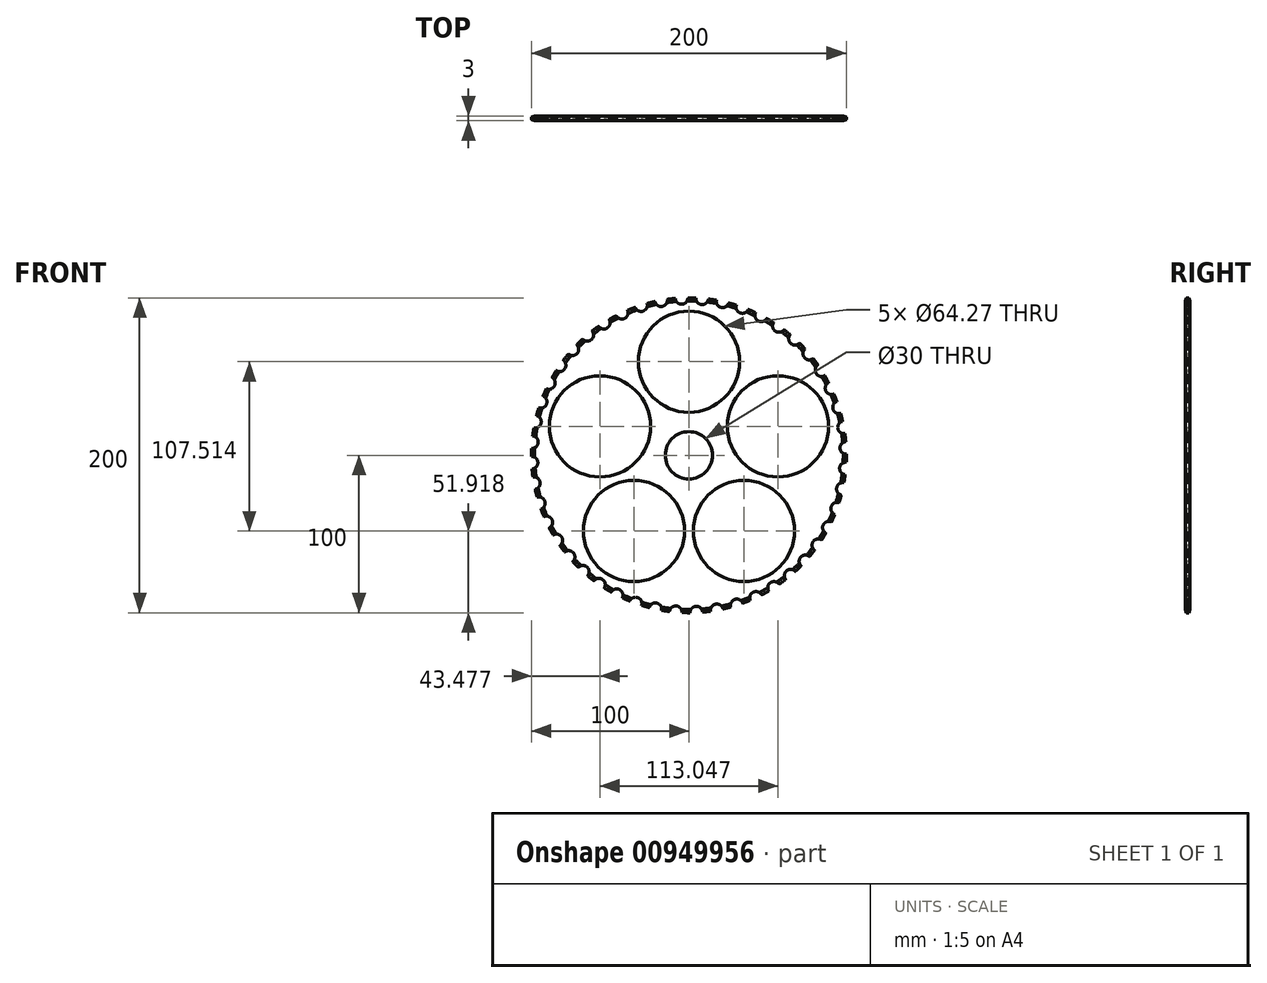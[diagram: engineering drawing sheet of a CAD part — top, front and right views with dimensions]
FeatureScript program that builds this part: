
annotation { "Feature Type Name" : "Feature", "Feature Type Description" : "" }
export const myFeature = defineFeature(function(context is Context, id is Id, definition is map)
    precondition{}
    {
        {
            var Q0;
            Q0=qCreatedBy(makeId("Front.planeOp"),FACE);
            var sketch = newSketch(context, id + "F0", { "sketchPlane" : qUnion([Q0])});
            skCircle(sketch, "E0", {"center": v(0, 0) * mm, "radius": 100 * mm});
            skCircle(sketch, "E1", {"center": v(0, 59.43) * mm, "radius": 32.14 * mm});
            skCircle(sketch, "E2.1.0", {"center": v(-56.52, 18.37) * mm, "radius": 32.14 * mm});
            skCircle(sketch, "E2.2.0", {"center": v(-34.93, -48.08) * mm, "radius": 32.14 * mm});
            skCircle(sketch, "E2.3.0", {"center": v(34.93, -48.08) * mm, "radius": 32.14 * mm});
            skCircle(sketch, "E2.4.0", {"center": v(56.52, 18.37) * mm, "radius": 32.14 * mm});
            skSolve(sketch);
        }
        {
            var Q0;
            Q0=makeQuery(id+"F0.imprint","IMPRINT",FACE,{"disambiguationData":[TD([[makeQuery(id+"F0.imprint","IMPRINT",EDGE,{"derivedFrom":sQuery(id+"F0.wireOp",EDGE,"E0")}),1.0]])]});
            extrude(context, id + "F1", {"entities" : qUnion([Q0]), "depth" : 3 * mm, "offsetDistance" : 25 * mm});
        }
        {
            var Q0;
            {var subQ0=sQuery(id+"F0.wireOp",EDGE,"E0");Q0=makeQuery(id+"FjPS6zSCau8WYdw_1.boolean.opBoolean","SPLIT",EDGE,{"disambiguationData":[TD([makeQuery(id+"F1.opExtrude","SWEPT_FACE",FACE,{"disambiguationData":[OSD([subQ0])]}),makeQuery(id+"F1.opExtrude","CAP_FACE",FACE,{"disambiguationData":[OSD([subQ0])],"isStart":false}),makeQuery(id+"FjPS6zSCau8WYdw_1.opExtrude","SWEPT_FACE",FACE,{"disambiguationData":[OSD([sQuery(id+"F4.wireOp",EDGE,"E4.5.0")])]}),makeQuery(id+"FjPS6zSCau8WYdw_1.opExtrude","SWEPT_FACE",FACE,{"disambiguationData":[OSD([sQuery(id+"F4.wireOp",EDGE,"E4.6.0")])]})])],"derivedFrom":makeQuery(id+"F1.opExtrude","CAP_EDGE",EDGE,{"disambiguationData":[OSD([subQ0])],"isStart":false})});}
            chamfer(context, id + "F2", {"entities" : qUnion([Q0]), "chamferType" : ChamferType.TWO_OFFSETS, "width1" : 2 * mm, "oppositeDirection" : false, "width2" : 0.75 * mm, "tangentPropagation" : true});
        }
        {
            var Q0;
            {var subQ0=sQuery(id+"F0.wireOp",EDGE,"E0");Q0=makeQuery(id+"FjPS6zSCau8WYdw_1.boolean.opBoolean","SPLIT",EDGE,{"disambiguationData":[TD([makeQuery(id+"F1.opExtrude","SWEPT_FACE",FACE,{"disambiguationData":[OSD([subQ0])]}),makeQuery(id+"F1.opExtrude","CAP_FACE",FACE,{"disambiguationData":[OSD([subQ0])],"isStart":true}),makeQuery(id+"FjPS6zSCau8WYdw_1.opExtrude","SWEPT_FACE",FACE,{"disambiguationData":[OSD([sQuery(id+"F4.wireOp",EDGE,"E4.21.0")])]}),makeQuery(id+"FjPS6zSCau8WYdw_1.opExtrude","SWEPT_FACE",FACE,{"disambiguationData":[OSD([sQuery(id+"F4.wireOp",EDGE,"E4.22.0")])]})])],"derivedFrom":makeQuery(id+"F1.opExtrude","CAP_EDGE",EDGE,{"disambiguationData":[OSD([subQ0])],"isStart":true})});}
            chamfer(context, id + "F3", {"entities" : qUnion([Q0]), "chamferType" : ChamferType.TWO_OFFSETS, "width1" : 0.75 * mm, "oppositeDirection" : false, "width2" : 2 * mm, "tangentPropagation" : true});
        }
        {
            var Q0;
            Q0=makeQuery(id+"F1.opExtrude","CAP_FACE",FACE,{"disambiguationData":[OSD([sQuery(id+"F0.wireOp",EDGE,"E0")])],"isStart":false});
            var sketch = newSketch(context, id + "F4", { "sketchPlane" : qUnion([Q0])});
            skCircle(sketch, "E3", {"center": v(-88.92, 45.9) * mm, "radius": 4 * mm});
            skCircle(sketch, "E4.1.0", {"center": v(-94.15, 33.9) * mm, "radius": 4 * mm});
            skCircle(sketch, "E4.2.0", {"center": v(-97.77, 21.33) * mm, "radius": 4 * mm});
            skCircle(sketch, "E4.3.0", {"center": v(-99.72, 8.38) * mm, "radius": 4 * mm});
            skCircle(sketch, "E4.4.0", {"center": v(-99.96, -4.7) * mm, "radius": 4 * mm});
            skCircle(sketch, "E4.5.0", {"center": v(-98.49, -17.7) * mm, "radius": 4 * mm});
            skCircle(sketch, "E4.6.0", {"center": v(-95.33, -30.41) * mm, "radius": 4 * mm});
            skCircle(sketch, "E4.7.0", {"center": v(-90.55, -42.6) * mm, "radius": 4 * mm});
            skCircle(sketch, "E4.8.0", {"center": v(-84.21, -54.05) * mm, "radius": 4 * mm});
            skCircle(sketch, "E4.9.0", {"center": v(-76.44, -64.58) * mm, "radius": 4 * mm});
            skCircle(sketch, "E4.10.0", {"center": v(-67.35, -74) * mm, "radius": 4 * mm});
            skCircle(sketch, "E4.11.0", {"center": v(-57.12, -82.16) * mm, "radius": 4 * mm});
            skCircle(sketch, "E4.12.0", {"center": v(-45.9, -88.92) * mm, "radius": 4 * mm});
            skCircle(sketch, "E4.13.0", {"center": v(-33.9, -94.15) * mm, "radius": 4 * mm});
            skCircle(sketch, "E4.14.0", {"center": v(-21.33, -97.77) * mm, "radius": 4 * mm});
            skCircle(sketch, "E4.15.0", {"center": v(-8.38, -99.72) * mm, "radius": 4 * mm});
            skCircle(sketch, "E4.16.0", {"center": v(4.7, -99.96) * mm, "radius": 4 * mm});
            skCircle(sketch, "E4.17.0", {"center": v(17.7, -98.49) * mm, "radius": 4 * mm});
            skCircle(sketch, "E4.18.0", {"center": v(30.41, -95.33) * mm, "radius": 4 * mm});
            skCircle(sketch, "E4.19.0", {"center": v(42.6, -90.55) * mm, "radius": 4 * mm});
            skCircle(sketch, "E4.20.0", {"center": v(54.05, -84.21) * mm, "radius": 4 * mm});
            skCircle(sketch, "E4.21.0", {"center": v(64.58, -76.44) * mm, "radius": 4 * mm});
            skCircle(sketch, "E4.22.0", {"center": v(74, -67.35) * mm, "radius": 4 * mm});
            skCircle(sketch, "E4.23.0", {"center": v(82.16, -57.12) * mm, "radius": 4 * mm});
            skCircle(sketch, "E4.24.0", {"center": v(88.92, -45.9) * mm, "radius": 4 * mm});
            skCircle(sketch, "E4.25.0", {"center": v(94.15, -33.9) * mm, "radius": 4 * mm});
            skCircle(sketch, "E4.26.0", {"center": v(97.77, -21.33) * mm, "radius": 4 * mm});
            skCircle(sketch, "E4.27.0", {"center": v(99.72, -8.38) * mm, "radius": 4 * mm});
            skCircle(sketch, "E4.28.0", {"center": v(99.96, 4.7) * mm, "radius": 4 * mm});
            skCircle(sketch, "E4.29.0", {"center": v(98.49, 17.7) * mm, "radius": 4 * mm});
            skCircle(sketch, "E4.30.0", {"center": v(95.33, 30.41) * mm, "radius": 4 * mm});
            skCircle(sketch, "E4.31.0", {"center": v(90.55, 42.6) * mm, "radius": 4 * mm});
            skCircle(sketch, "E4.32.0", {"center": v(84.21, 54.05) * mm, "radius": 4 * mm});
            skCircle(sketch, "E4.33.0", {"center": v(76.44, 64.58) * mm, "radius": 4 * mm});
            skCircle(sketch, "E4.34.0", {"center": v(67.35, 74) * mm, "radius": 4 * mm});
            skCircle(sketch, "E4.35.0", {"center": v(57.12, 82.16) * mm, "radius": 4 * mm});
            skCircle(sketch, "E4.36.0", {"center": v(45.9, 88.92) * mm, "radius": 4 * mm});
            skCircle(sketch, "E4.37.0", {"center": v(33.9, 94.15) * mm, "radius": 4 * mm});
            skCircle(sketch, "E4.38.0", {"center": v(21.33, 97.77) * mm, "radius": 4 * mm});
            skCircle(sketch, "E4.39.0", {"center": v(8.38, 99.72) * mm, "radius": 4 * mm});
            skCircle(sketch, "E4.40.0", {"center": v(-4.7, 99.96) * mm, "radius": 4 * mm});
            skCircle(sketch, "E4.41.0", {"center": v(-17.7, 98.49) * mm, "radius": 4 * mm});
            skCircle(sketch, "E4.42.0", {"center": v(-30.41, 95.33) * mm, "radius": 4 * mm});
            skCircle(sketch, "E4.43.0", {"center": v(-42.6, 90.55) * mm, "radius": 4 * mm});
            skCircle(sketch, "E4.44.0", {"center": v(-54.05, 84.21) * mm, "radius": 4 * mm});
            skCircle(sketch, "E4.45.0", {"center": v(-64.58, 76.44) * mm, "radius": 4 * mm});
            skCircle(sketch, "E4.46.0", {"center": v(-74, 67.35) * mm, "radius": 4 * mm});
            skCircle(sketch, "E4.47.0", {"center": v(-82.16, 57.12) * mm, "radius": 4 * mm});
            skPoint(sketch, "E4.center", {"position": v(0, 0) * mm});
            skCircle(sketch, "E5", {"center": v(0, 0) * mm, "radius": 15 * mm});
            skCircle(sketch, "E6", {"center": v(0, 0) * mm, "radius": 24.55 * mm, "construction": true});
            skCircle(sketch, "E7", {"center": v(0, 0) * mm, "radius": 106.64 * mm, "construction": true});
            skLineSegment(sketch, "E8", {"start": v(0, 115.3) * mm, "end": v(0, -115.73) * mm, "construction": true});
            skLineSegment(sketch, "E9", {"start": v(-114.53, 0) * mm, "end": v(114.1, 0) * mm, "construction": true});
            skLineSegment(sketch, "E10.1.0", {"start": v(-80.99, -80.99) * mm, "end": v(80.68, 80.68) * mm, "construction": true});
            skLineSegment(sketch, "E10.2.0", {"start": v(0, -114.53) * mm, "end": v(0, 114.1) * mm, "construction": true});
            skLineSegment(sketch, "E10.3.0", {"start": v(80.99, -80.99) * mm, "end": v(-80.68, 80.68) * mm, "construction": true});
            skLineSegment(sketch, "E10.4.0", {"start": v(-29.05, 0) * mm, "end": v(-78.54, 0) * mm, "construction": true});
            skLineSegment(sketch, "E10.5.0", {"start": v(80.99, 80.99) * mm, "end": v(-80.68, -80.68) * mm, "construction": true});
            skLineSegment(sketch, "E10.6.0", {"start": v(0, 114.53) * mm, "end": v(0, -114.1) * mm, "construction": true});
            skLineSegment(sketch, "E10.7.0", {"start": v(-56.1, 56.1) * mm, "end": v(-20.44, 20.44) * mm, "construction": true});
            skLineSegment(sketch, "E11", {"start": v(-59.84, 59.84) * mm, "end": v(-17.36, 17.36) * mm});
            skLineSegment(sketch, "E12", {"start": v(-24.55, 0) * mm, "end": v(-83.68, 0) * mm});
            skPoint(sketch, "E13.1.internal.snap0", {"position": v(-20.96, 8.68) * mm});
            skPoint(sketch, "E14.newPointB", {"position": v(-80.99, 80.99) * mm});
            skPoint(sketch, "E15.newPointB", {"position": v(-114.1, 0) * mm});
            skPoint(sketch, "E16.newPointB", {"position": v(114.53, 0) * mm});
            skPoint(sketch, "E17.newPointB", {"position": v(80.68, -80.68) * mm});
            skLineSegment(sketch, "E18.1.0", {"start": v(-20.53, -76.62) * mm, "end": v(-7.48, -27.92) * mm, "construction": true});
            skLineSegment(sketch, "E18.2.0", {"start": v(76.62, 20.53) * mm, "end": v(27.92, 7.48) * mm, "construction": true});
            skSolve(sketch);
        }
        {
            var Q0;
            Q0 = qSketchRegion(id + "F4", true);
            extrude(context, id + "F5", {"entities" : qUnion([Q0]), "operationType" : NewBodyOperationType.REMOVE, "endBound" : BoundingType.THROUGH_ALL, "oppositeDirection" : true, "depth" : 25 * mm, "offsetDistance" : 25 * mm});
        }
    });
